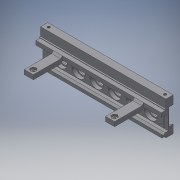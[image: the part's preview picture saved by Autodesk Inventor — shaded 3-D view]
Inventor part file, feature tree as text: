
AUTODESK INVENTOR PART (.ipt)
format: ipt  version: 2016 SP2 (Build 200236200, 236)  size: 311,296 bytes
history: native  units: mm
features: reference x16, extrude x9, sketch x9, chamfer x2, mirror x1, pattern_linear x1
ambient origin geometry x8: Origin, YZ Plane, XZ Plane, XY Plane, X Axis, Y Axis, Z Axis, Center Point
bodies: Volumenkörper1 (feature_tree)
feature tree (38):
  extrude  "Extrusion1"  Depth=4.5mm
  extrude  "Extrusion2"  Depth=3.5mm
  extrude  "Extrusion3"  Depth=15.97mm
  chamfer  "Fase1"  Distance=69.4mm
  chamfer  "Fase2"  Distance=5.0mm
  extrude  "Extrusion4"  Depth=2.0mm TaperAngle=45.0deg
  extrude  "Extrusion5"  Depth=2.0mm TaperAngle=45.0deg
  extrude  "Extrusion6"  Depth=3.5mm
  mirror  "Spiegeln1"
  extrude  "Extrusion9"  Depth=5.0mm
  extrude  "Extrusion10"  Depth=5.0mm
  extrude  "Extrusion11"  Depth=32.25mm TaperAngle=0.0deg
  pattern_linear  "Rechteckige Anordnung1"  Spacing1=34.75mm  [1 undecoded]
  sketch  "Skizze1"  dims[d0=2.0mm d1=4.5mm]
  reference  "Referenz1"
  reference  "Referenz2"
  reference  "Referenz3"
  reference  "Referenz4"
  reference  "Referenz5"
  reference  "Referenz6"
  reference  "Referenz7"
  reference  "Referenz8"
  reference  "Referenz9"
  sketch  "Skizze2"  dims[d2=3.5mm d3=3.47mm]
  reference  "Referenz10"
  sketch  "Skizze3"  dims[d4=15.97mm d5=1.8mm]
  reference  "Referenz11"
  sketch  "Skizze4"  dims[d6=45.0deg]
  sketch  "Skizze6"  dims[d7=135.0deg]
  sketch  "Skizze7"  dims[d8=4.53mm]
  sketch  "Skizze10"  dims[d9=1.8mm]
  reference  "Referenz15"
  reference  "Referenz16"
  reference  "Referenz17"
  reference  "Referenz18"
  sketch  "Skizze11"  dims[d10=4.5mm d11=69.4mm d12=0.0mm d13=5.0mm d14=0.0mm]
  sketch  "Skizze12"  dims[d15=32.25mm d16=0.0mm d17=2.4mm d18=2.0mm d19=45.0deg d20=2.0mm d21=2.0mm d22=45.0deg d23=3.5mm d24=5.0mm d25=5.0mm d26=32.25mm d27=0.0mm d28=34.75mm d29=0.0mm d30=11.25mm d31=0.0mm d51=5.7mm d52=5.7mm d53=2.2mm d54=0.0mm d61=12.0mm d62=19.4mm d63=5.5mm d64=0.0mm d65=15.0mm d66=4.0mm d67=0.0mm d68=60.0mm d70=20.0mm d71=5.43mm]
  reference  "Referenz19"
note: 1 required parameter value undecoded (feature->parameter linkage not recoverable at this tier; creation-order binding heuristic only, values carry confidence <= 0.55)
